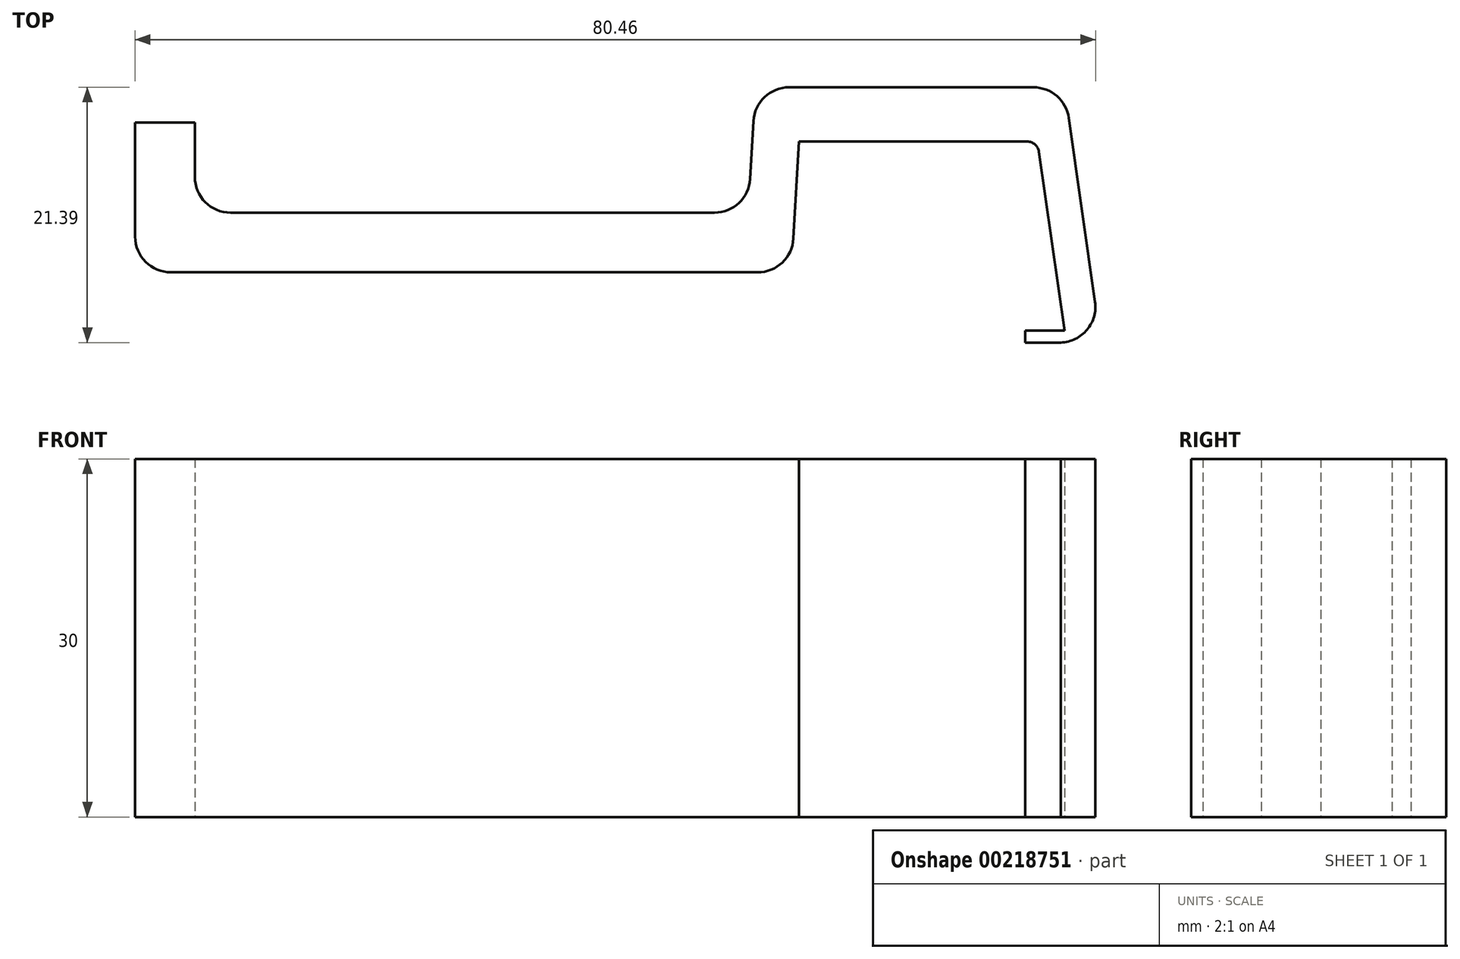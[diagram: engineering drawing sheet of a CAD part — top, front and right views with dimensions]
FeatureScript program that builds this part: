
annotation { "Feature Type Name" : "Feature", "Feature Type Description" : "" }
export const myFeature = defineFeature(function(context is Context, id is Id, definition is map)
    precondition{}
    {
        {
            var Q0;
            Q0=qCreatedBy(makeId("Top.planeOp"),FACE);
            var sketch = newSketch(context, id + "F0", { "sketchPlane" : qUnion([Q0])});
            skLineSegment(sketch, "E0", {"start": v(-47.86, -10.96) * mm, "end": v(1.3, -10.96) * mm});
            skLineSegment(sketch, "E1", {"start": v(4.3, -8.12) * mm, "end": v(4.74, -0.15) * mm});
            skLineSegment(sketch, "E2", {"start": v(9.38, 0) * mm, "end": v(23.88, 0) * mm});
            skLineSegment(sketch, "E3", {"start": v(24.87, -0.86) * mm, "end": v(27, -15.84) * mm});
            skLineSegment(sketch, "E4", {"start": v(27, -15.84) * mm, "end": v(26.7, -15.84) * mm});
            skLineSegment(sketch, "E5", {"start": v(26.7, -15.84) * mm, "end": v(26.7, -16.84) * mm});
            skLineSegment(sketch, "E6", {"start": v(26.6, -16.84) * mm, "end": v(26.7, -16.84) * mm});
            skLineSegment(sketch, "E7", {"start": v(29.57, -13.42) * mm, "end": v(27.37, 1.97) * mm});
            skLineSegment(sketch, "E8", {"start": v(24.4, 4.55) * mm, "end": v(3.93, 4.55) * mm});
            skLineSegment(sketch, "E9", {"start": v(0.94, 1.71) * mm, "end": v(0.67, -3.12) * mm});
            skLineSegment(sketch, "E10", {"start": v(-2.33, -5.96) * mm, "end": v(-42.86, -5.96) * mm});
            skLineSegment(sketch, "E11", {"start": v(-45.86, -2.96) * mm, "end": v(-45.86, 1.6) * mm});
            skLineSegment(sketch, "E12", {"start": v(-45.86, 1.6) * mm, "end": v(-50.86, 1.6) * mm});
            skLineSegment(sketch, "E13", {"start": v(-50.86, 1.6) * mm, "end": v(-50.86, -7.96) * mm});
            skPoint(sketch, "E14.visualSharp", {"position": v(-45.86, -5.96) * mm});
            skArc(sketch, "E14.filletArc", {"start": v(-45.86, -2.96) * mm, "mid": v(-44.98, -5.08) * mm, "end": v(-42.86, -5.96) * mm});
            skPoint(sketch, "E15.visualSharp", {"position": v(-50.86, -10.96) * mm});
            skArc(sketch, "E15.filletArc", {"start": v(-50.86, -7.96) * mm, "mid": v(-49.98, -10.08) * mm, "end": v(-47.86, -10.96) * mm});
            skPoint(sketch, "E16.visualSharp", {"position": v(4.14, -10.96) * mm});
            skArc(sketch, "E16.filletArc", {"start": v(1.3, -10.96) * mm, "mid": v(3.36, -10.14) * mm, "end": v(4.3, -8.12) * mm});
            skPoint(sketch, "E17.visualSharp", {"position": v(0.51, -5.96) * mm});
            skArc(sketch, "E17.filletArc", {"start": v(-2.33, -5.96) * mm, "mid": v(-0.26, -5.14) * mm, "end": v(0.67, -3.12) * mm});
            skPoint(sketch, "E18.visualSharp", {"position": v(1.1, 4.55) * mm});
            skArc(sketch, "E18.filletArc", {"start": v(3.93, 4.55) * mm, "mid": v(1.87, 3.73) * mm, "end": v(0.94, 1.71) * mm});
            skPoint(sketch, "E19.visualSharp", {"position": v(27, 4.55) * mm});
            skArc(sketch, "E19.filletArc", {"start": v(27.37, 1.97) * mm, "mid": v(26.37, 3.81) * mm, "end": v(24.4, 4.55) * mm});
            skPoint(sketch, "E20.visualSharp", {"position": v(30.05, -16.84) * mm});
            skArc(sketch, "E20.filletArc", {"start": v(26.6, -16.84) * mm, "mid": v(28.86, -15.8) * mm, "end": v(29.57, -13.42) * mm});
            skPoint(sketch, "E21.visualSharp", {"position": v(4.74, 0) * mm});
            skLineSegment(sketch, "E22", {"start": v(4.74, 0) * mm, "end": v(4.74, -0.15) * mm});
            skLineSegment(sketch, "E23", {"start": v(4.74, 0) * mm, "end": v(9.38, 0) * mm});
            skPoint(sketch, "E24.visualSharp", {"position": v(24.74, 0) * mm});
            skArc(sketch, "E24.filletArc", {"start": v(24.87, -0.86) * mm, "mid": v(24.53, -0.24) * mm, "end": v(23.88, 0) * mm});
            skSolve(sketch);
        }
        {
            var Q0;
            Q0=makeQuery(id+"F0.imprint","IMPRINT",FACE,{"disambiguationData":[TD([[makeQuery(id+"F0.imprint","IMPRINT",EDGE,{"derivedFrom":sQuery(id+"F0.wireOp",EDGE,"E0")}),1.0]])]});
            extrude(context, id + "F1", {"entities" : qUnion([Q0]), "depth" : 30 * mm});
        }
        {
            var Q0;
            Q0=makeQuery(id+"F1.opExtrude","SWEPT_FACE",FACE,{"disambiguationData":[OSD([sQuery(id+"F0.wireOp",EDGE,"E5")])]});
            extrude(context, id + "F2", {"entities" : qUnion([Q0]), "operationType" : NewBodyOperationType.ADD, "depth" : 3 * mm, "offsetDistance" : 25 * mm});
        }
    });
